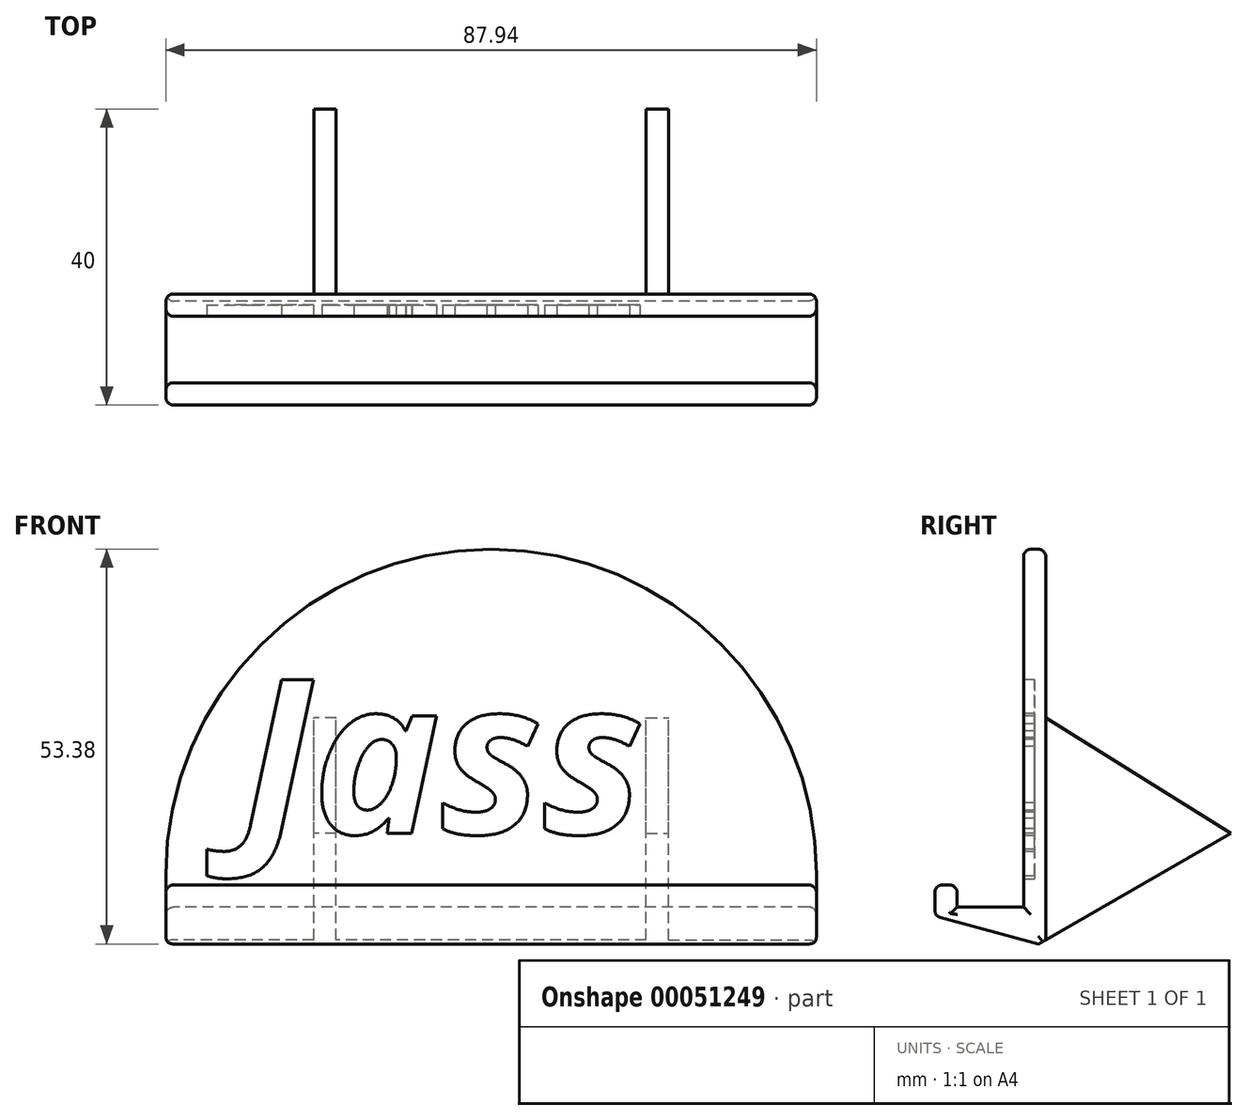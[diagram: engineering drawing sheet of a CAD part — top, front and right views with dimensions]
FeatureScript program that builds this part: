
annotation { "Feature Type Name" : "Feature", "Feature Type Description" : "" }
export const myFeature = defineFeature(function(context is Context, id is Id, definition is map)
    precondition{}
    {
        {
            assignVariable(context, id + "F0", {"name" : "thickness", "anyValue" : 3});
        }
        {
            assignVariable(context, id + "F1", {"name" : "leg_depth", "anyValue" : 25});
        }
        {
            var Q0;
            Q0=qCreatedBy(makeId("Front.planeOp"),FACE);
            var sketch = newSketch(context, id + "F2", { "sketchPlane" : qUnion([Q0])});
            skArc(sketch, "E0", {"start": v(0, 43.97) * mm, "mid": v(-31.09, 31.09) * mm, "end": v(-43.97, 0) * mm});
            skLineSegment(sketch, "E1", {"start": v(0, 43.97) * mm, "end": v(0, -8.86) * mm});
            skLineSegment(sketch, "E2", {"start": v(0, -8.86) * mm, "end": v(-43.97, -8.86) * mm});
            skLineSegment(sketch, "E3", {"start": v(-43.97, -8.86) * mm, "end": v(-43.97, 0) * mm});
            skSolve(sketch);
        }
        {
            var Q0;
            Q0=makeQuery(id+"F2.imprint","IMPRINT",FACE,{"disambiguationData":[TD([[makeQuery(id+"F2.imprint","IMPRINT",EDGE,{"derivedFrom":sQuery(id+"F2.wireOp",EDGE,"E0")}),1.0]])]});
            extrude(context, id + "F3", {"entities" : qUnion([Q0]), "depth" : (getVariable(context, 'thickness')) * mm});
        }
        {
            var Q0;
            Q0=makeQuery(id+"F3.opExtrude","CAP_FACE",FACE,{"disambiguationData":[OSD([sQuery(id+"F2.wireOp",EDGE,"E0"),sQuery(id+"F2.wireOp",EDGE,"E1"),sQuery(id+"F2.wireOp",EDGE,"E2"),sQuery(id+"F2.wireOp",EDGE,"E3")])],"isStart":true});
            var sketch = newSketch(context, id + "F4", { "sketchPlane" : qUnion([Q0])});
            skLineSegment(sketch, "E4.bottom", {"start": v(20.97, -8.86) * mm, "end": v(23.97, -8.86) * mm});
            skLineSegment(sketch, "E4.top", {"start": v(20.97, 21.14) * mm, "end": v(23.97, 21.14) * mm});
            skLineSegment(sketch, "E4.left", {"start": v(20.97, -8.86) * mm, "end": v(20.97, 21.14) * mm});
            skLineSegment(sketch, "E4.right", {"start": v(23.97, -8.86) * mm, "end": v(23.97, 21.14) * mm});
            skSolve(sketch);
        }
        {
            var Q0;
            Q0=makeQuery(id+"F4.imprint","IMPRINT",FACE,{"disambiguationData":[TD([[makeQuery(id+"F4.imprint","IMPRINT",EDGE,{"derivedFrom":sQuery(id+"F4.wireOp",EDGE,"E4.bottom")}),1.0]])]});
            extrude(context, id + "F5", {"entities" : qUnion([Q0]), "operationType" : NewBodyOperationType.ADD, "depth" : (getVariable(context, 'leg_depth')) * mm});
        }
        {
            var Q0;
            Q0=makeQuery(id+"F5.opExtrude","SWEPT_FACE",FACE,{"disambiguationData":[OSD([sQuery(id+"F4.wireOp",EDGE,"E4.right")])]});
            var sketch = newSketch(context, id + "F6", { "sketchPlane" : qUnion([Q0])});
            skLineSegment(sketch, "E5", {"start": v(0, -8.86) * mm, "end": v(-25, 5.58) * mm});
            skLineSegment(sketch, "E6", {"start": v(-25, 5.58) * mm, "end": v(0, 21.14) * mm});
            skSolve(sketch);
        }
        {
            var Q0;
            {var subQ0=sQuery(id+"F6.wireOp",EDGE,"E6");Q0=makeQuery(id+"F6.imprint","IMPRINT",FACE,{"disambiguationData":[TD([[makeQuery(id+"F6.imprint","IMPRINT",EDGE,{"derivedFrom":subQ0}),1.0]])]});}
            var Q1;
            {var subQ0=sQuery(id+"F6.wireOp",EDGE,"E5");Q1=makeQuery(id+"F6.imprint","IMPRINT",FACE,{"disambiguationData":[TD([[makeQuery(id+"F6.imprint","IMPRINT",EDGE,{"derivedFrom":subQ0}),1.0]])]});}
            extrude(context, id + "F7", {"entities" : qUnion([Q0, Q1]), "operationType" : NewBodyOperationType.REMOVE, "endBound" : BoundingType.UP_TO_NEXT, "oppositeDirection" : true, "depth" : 25 * mm});
        }
        {
            var Q0;
            Q0=makeQuery(id+"F3.opExtrude","SWEPT_FACE",FACE,{"disambiguationData":[OSD([sQuery(id+"F2.wireOp",EDGE,"E3")])]});
            var sketch = newSketch(context, id + "F8", { "sketchPlane" : qUnion([Q0])});
            skLineSegment(sketch, "E7", {"start": v(3, -4.43) * mm, "end": v(12, -4.43) * mm});
            skLineSegment(sketch, "E8", {"start": v(12, -4.43) * mm, "end": v(12, -1.43) * mm});
            skLineSegment(sketch, "E9", {"start": v(12, -1.43) * mm, "end": v(15, -1.43) * mm});
            skLineSegment(sketch, "E10", {"start": v(15, -5.64) * mm, "end": v(0.95, -9.4) * mm});
            skLineSegment(sketch, "E11", {"start": v(0.95, -9.4) * mm, "end": v(0, -8.86) * mm});
            skLineSegment(sketch, "E12", {"start": v(15, -1.43) * mm, "end": v(15, -5.64) * mm});
            skPoint(sketch, "E13", {"position": v(3, -8.86) * mm});
            skSolve(sketch);
        }
        {
            var Q0;
            {var subQ3=sQuery(id+"F8.wireOp",EDGE,"E11");Q0=makeQuery(id+"F8.imprint","IMPRINT",FACE,{"disambiguationData":[TD([[makeQuery(id+"F8.imprint","IMPRINT",EDGE,{"derivedFrom":subQ3}),-1.0]])]});}
            var Q1;
            {var subQ5=sQuery(id+"F8.wireOp",EDGE,"E7");Q1=makeQuery(id+"F8.imprint","IMPRINT",FACE,{"disambiguationData":[TD([[makeQuery(id+"F8.imprint","IMPRINT",EDGE,{"derivedFrom":subQ5}),-1.0]])]});}
            var Q2;
            Q2=makeQuery(id+"F3.opExtrude","SWEPT_FACE",FACE,{"disambiguationData":[OSD([sQuery(id+"F2.wireOp",EDGE,"E1")])]});
            extrude(context, id + "F9", {"entities" : qUnion([Q0, Q1]), "operationType" : NewBodyOperationType.ADD, "endBound" : BoundingType.UP_TO_SURFACE, "oppositeDirection" : true, "endBoundEntityFace" : qUnion([Q2]), "depth" : 25 * mm});
        }
        {
            var Q0;
            Q0=makeQuery(id+"F9.opExtrude","SWEPT_EDGE",EDGE,{"disambiguationData":[OSD([sQuery(id+"F8.wireOp",EDGE,"E10"),sQuery(id+"F8.wireOp",EDGE,"E12")])]});
            var Q1;
            Q1=makeQuery(id+"F9.opExtrude","SWEPT_EDGE",EDGE,{"disambiguationData":[OSD([sQuery(id+"F8.wireOp",EDGE,"E9"),sQuery(id+"F8.wireOp",EDGE,"E12")])]});
            var Q2;
            Q2=makeQuery(id+"F9.opExtrude","SWEPT_EDGE",EDGE,{"disambiguationData":[OSD([sQuery(id+"F8.wireOp",EDGE,"E8"),sQuery(id+"F8.wireOp",EDGE,"E9")])]});
            var Q3;
            Q3=makeQuery(id+"F3.opExtrude","CAP_EDGE",EDGE,{"disambiguationData":[OSD([sQuery(id+"F2.wireOp",EDGE,"E0")])],"isStart":false});
            var Q4;
            Q4=makeQuery(id+"F3.opExtrude","CAP_EDGE",EDGE,{"disambiguationData":[OSD([sQuery(id+"F2.wireOp",EDGE,"E0")])],"isStart":true});
            var Q5;
            {var subQ0=sQuery(id+"F8.wireOp",EDGE,"E10");Q5=makeQuery(id+"F9.boolean.opBoolean","MERGE",EDGE,{"derivedFrom":[makeQuery(id+"F9.opExtrude","CAP_EDGE",EDGE,{"disambiguationData":[OSD([subQ0]),TDD([makeQuery(id+"F8.imprint","IMPRINT",EDGE,{"disambiguationData":[TD([[makeQuery(id+"F8.imprint","INTERSECT",VERTEX,{"derivedFrom":[subQ0,sQuery(id+"F8.wireOp",EDGE,"E12")]}),-1.0]])],"derivedFrom":subQ0})])],"isStart":true}),makeQuery(id+"F9.opExtrude","CAP_EDGE",EDGE,{"disambiguationData":[OSD([subQ0]),TDD([makeQuery(id+"F8.imprint","IMPRINT",EDGE,{"disambiguationData":[TD([[makeQuery(id+"F8.imprint","INTERSECT",VERTEX,{"derivedFrom":[subQ0,sQuery(id+"F8.wireOp",EDGE,"E11")]}),1.0]])],"derivedFrom":subQ0})])],"isStart":true})]});}
            var Q6;
            Q6=makeQuery(id+"F3.opExtrude","CAP_EDGE",EDGE,{"disambiguationData":[OSD([sQuery(id+"F2.wireOp",EDGE,"E3")])],"isStart":true});
            var Q7;
            {var subQ0=sQuery(id+"F4.wireOp",EDGE,"E4.top");Q7=makeQuery(id+"F7.boolean.opBoolean","MERGE",EDGE,{"derivedFrom":[makeQuery(id+"F5.opExtrude","CAP_EDGE",EDGE,{"disambiguationData":[OSD([subQ0])],"isStart":true})],"fromTools":[makeQuery(id+"F7.opExtrude","SWEPT_EDGE",EDGE,{"disambiguationData":[OSD([subQ0,sQuery(id+"F4.wireOp",EDGE,"E4.right"),sQuery(id+"F6.wireOp",EDGE,"E6")])]})]});}
            var Q8;
            Q8=makeQuery(id+"F5.opExtrude","CAP_EDGE",EDGE,{"disambiguationData":[OSD([sQuery(id+"F4.wireOp",EDGE,"E4.right")])],"isStart":true});
            var Q9;
            Q9=makeQuery(id+"F5.opExtrude","CAP_EDGE",EDGE,{"disambiguationData":[OSD([sQuery(id+"F4.wireOp",EDGE,"E4.left")])],"isStart":true});
            var Q10;
            Q10=makeQuery(id+"F7.boolean.opBoolean","COPY",EDGE,{"derivedFrom":makeQuery(id+"F7.opExtrude","CAP_EDGE",EDGE,{"disambiguationData":[OSD([sQuery(id+"F6.wireOp",EDGE,"E6")])],"isStart":true})});
            var Q11;
            Q11=makeQuery(id+"F7.boolean.opBoolean","COPY",EDGE,{"derivedFrom":makeQuery(id+"F7.opExtrude","CAP_EDGE",EDGE,{"disambiguationData":[OSD([sQuery(id+"F6.wireOp",EDGE,"E6")])],"isStart":false})});
            var Q12;
            Q12=makeQuery(id+"F9.opExtrude","CAP_EDGE",EDGE,{"disambiguationData":[OSD([sQuery(id+"F8.wireOp",EDGE,"E7")])],"isStart":true});
            var Q13;
            Q13=makeQuery(id+"F9.opExtrude","CAP_EDGE",EDGE,{"disambiguationData":[OSD([sQuery(id+"F8.wireOp",EDGE,"E8")])],"isStart":true});
            var Q14;
            Q14=makeQuery(id+"F9.opExtrude","CAP_EDGE",EDGE,{"disambiguationData":[OSD([sQuery(id+"F8.wireOp",EDGE,"E12")])],"isStart":true});
            var Q15;
            Q15=makeQuery(id+"F9.opExtrude","CAP_EDGE",EDGE,{"disambiguationData":[OSD([sQuery(id+"F8.wireOp",EDGE,"E9")])],"isStart":true});
            fillet(context, id + "F10", {"entities" : qUnion([Q0, Q1, Q2, Q3, Q4, Q5, Q6, Q7, Q8, Q9, Q10, Q11, Q12, Q13, Q14, Q15]), "radius" : 1 * mm, "tangentPropagation" : true, "allowEdgeOverflow" : false});
        }
        {
            var Q0;
            Q0=makeQuery(id+"F3.opExtrude","SWEPT_BODY",BODY,{"disambiguationData":[OSD([sQuery(id+"F2.wireOp",EDGE,"E0"),sQuery(id+"F2.wireOp",EDGE,"E1"),sQuery(id+"F2.wireOp",EDGE,"E2"),sQuery(id+"F2.wireOp",EDGE,"E3")])]});
            var Q1;
            {var subQ0=sQuery(id+"F8.wireOp",EDGE,"E10");var subQ1=sQuery(id+"F2.wireOp",EDGE,"E3");Q1=makeQuery(id+"F9.boolean.opBoolean","MERGE",FACE,{"derivedFrom":[makeQuery(id+"F3.opExtrude","SWEPT_FACE",FACE,{"disambiguationData":[OSD([sQuery(id+"F2.wireOp",EDGE,"E1")])]}),makeQuery(id+"F9.opExtrude","CAP_FACE",FACE,{"disambiguationData":[OSD([subQ1,sQuery(id+"F8.wireOp",EDGE,"E7"),sQuery(id+"F8.wireOp",EDGE,"E8"),sQuery(id+"F8.wireOp",EDGE,"E9"),subQ0,sQuery(id+"F8.wireOp",EDGE,"E12")])],"isStart":false}),makeQuery(id+"F9.opExtrude","CAP_FACE",FACE,{"disambiguationData":[OSD([sQuery(id+"F2.wireOp",EDGE,"E2"),subQ1,subQ0,sQuery(id+"F8.wireOp",EDGE,"E11")])],"isStart":false})]});}
            mirror(context, id + "F11", {"operationType" : NewBodyOperationType.ADD, "entities" : qUnion([Q0]), "mirrorPlane" : qUnion([Q1])});
        }
        {
            var Q0;
            {var subQ0=makeQuery(id+"F3.opExtrude","CAP_FACE",FACE,{"disambiguationData":[OSD([sQuery(id+"F2.wireOp",EDGE,"E0"),sQuery(id+"F2.wireOp",EDGE,"E1"),sQuery(id+"F2.wireOp",EDGE,"E2"),sQuery(id+"F2.wireOp",EDGE,"E3")])],"isStart":false});Q0=makeQuery(id+"F11.boolean.opBoolean","MERGE",FACE,{"derivedFrom":[subQ0,makeQuery(id+"F11.opPattern","COPY",FACE,{"derivedFrom":subQ0,"instanceName":"1"})]});}
            var sketch = newSketch(context, id + "F12", { "sketchPlane" : qUnion([Q0])});
            skText(sketch, "E14", { "text": "Jass", "fontName": "OpenSans-BoldItalic.ttf"});
            const initialGuessF12  = {"E14": [-0.03383, 0.00552, 1, 0, 0.02097]};
            skSetInitialGuess(sketch, initialGuessF12);
            skSolve(sketch);
        }
        {
            var Q0;
            Q0=makeQuery(id+"F12.imprint","IMPRINT",FACE,{"disambiguationData":[TD([[makeQuery(id+"F12.imprint","IMPRINT",EDGE,{"derivedFrom":sQuery(id+"F12.wireOp",EDGE,"E14.sketch_text.stroke-0")}),-1.0]])]});
            var Q1;
            Q1=makeQuery(id+"F12.imprint","IMPRINT",FACE,{"disambiguationData":[TD([[makeQuery(id+"F12.imprint","IMPRINT",EDGE,{"derivedFrom":sQuery(id+"F12.wireOp",EDGE,"E14.sketch_text.stroke-10")}),-1.0]])]});
            var Q2;
            Q2=makeQuery(id+"F12.imprint","IMPRINT",FACE,{"disambiguationData":[TD([[makeQuery(id+"F12.imprint","IMPRINT",EDGE,{"derivedFrom":sQuery(id+"F12.wireOp",EDGE,"E14.sketch_text.stroke-35")}),-1.0]])]});
            var Q3;
            Q3=makeQuery(id+"F12.imprint","IMPRINT",FACE,{"disambiguationData":[TD([[makeQuery(id+"F12.imprint","IMPRINT",EDGE,{"derivedFrom":sQuery(id+"F12.wireOp",EDGE,"E14.sketch_text.stroke-58")}),-1.0]])]});
            var Q4;
            Q4=makeQuery(id+"F12.imprint","IMPRINT",FACE,{"disambiguationData":[TD([[makeQuery(id+"F12.imprint","IMPRINT",EDGE,{"derivedFrom":sQuery(id+"F12.wireOp",EDGE,"E14.sketch_text.stroke-81")}),-1.0]])]});
            extrude(context, id + "F13", {"entities" : qUnion([Q0, Q1, Q2, Q3, Q4]), "operationType" : NewBodyOperationType.REMOVE, "oppositeDirection" : true, "depth" : 1.5 * mm});
        }
    });
